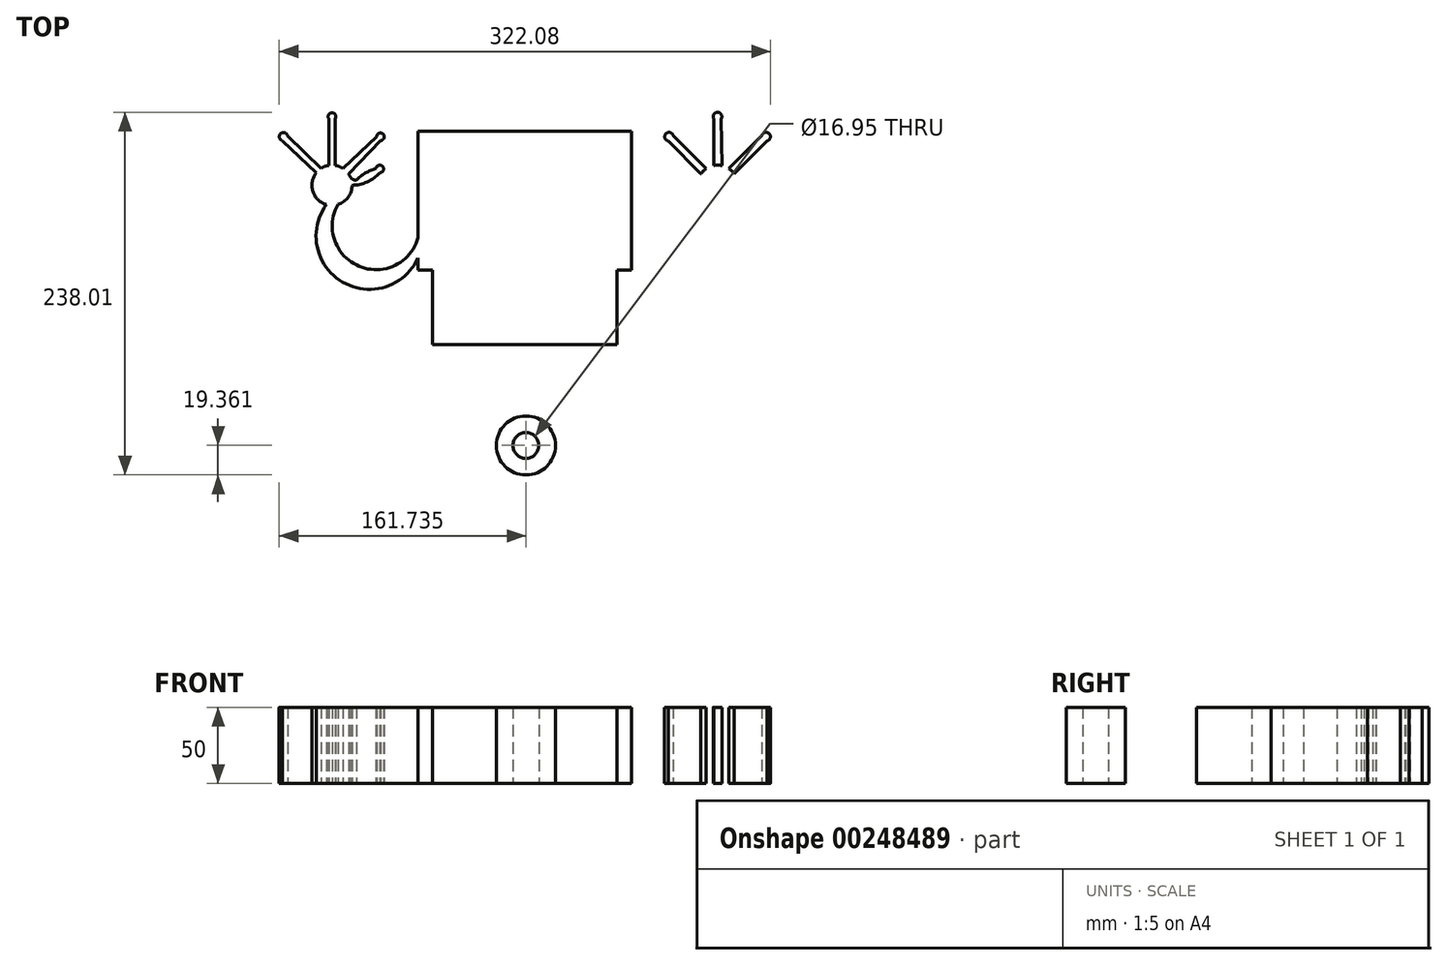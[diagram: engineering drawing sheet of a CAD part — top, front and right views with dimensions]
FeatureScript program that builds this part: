
annotation { "Feature Type Name" : "Feature", "Feature Type Description" : "" }
export const myFeature = defineFeature(function(context is Context, id is Id, definition is map)
    precondition{}
    {
        {
            var Q0;
            Q0=qCreatedBy(makeId("Top.planeOp"),FACE);
            var sketch = newSketch(context, id + "F0", { "sketchPlane" : qUnion([Q0])});
            skLineSegment(sketch, "E0.bottom", {"start": v(-60.5, -70) * mm, "end": v(60.5, -70) * mm});
            skLineSegment(sketch, "E0.top", {"start": v(-70, 70) * mm, "end": v(70, 70) * mm});
            skLineSegment(sketch, "E0.left", {"start": v(-70, -21.2) * mm, "end": v(-70, 70) * mm});
            skLineSegment(sketch, "E0.right", {"start": v(70, -21.2) * mm, "end": v(70, 70) * mm});
            skPoint(sketch, "E0.middle", {"position": v(0, 0) * mm});
            skLineSegment(sketch, "E1", {"start": v(-70, -21.2) * mm, "end": v(-60.5, -21.2) * mm});
            skLineSegment(sketch, "E2", {"start": v(-60.5, -21.2) * mm, "end": v(-60.5, -70) * mm});
            skLineSegment(sketch, "E3", {"start": v(0, -70) * mm, "end": v(0, -30.27) * mm, "construction": true});
            skPoint(sketch, "E3.endSnap0", {"position": v(0, -70) * mm});
            skLineSegment(sketch, "E4.MirrorCS", {"start": v(60.5, -21.2) * mm, "end": v(60.5, -70) * mm});
            skLineSegment(sketch, "E5.MirrorCS", {"start": v(70, -21.2) * mm, "end": v(60.5, -21.2) * mm});
            skArc(sketch, "E6", {"start": v(-130.05, 21.84) * mm, "mid": v(-119.54, -29.05) * mm, "end": v(-70, -13.35) * mm});
            skArc(sketch, "E7", {"start": v(-122.44, 21.94) * mm, "mid": v(-108.64, -18.7) * mm, "end": v(-70, 0) * mm});
            skArc(sketch, "E8.MirrorCS", {"start": v(122.44, 21.94) * mm, "mid": v(108.64, -18.7) * mm, "end": v(70, 0) * mm});
            skArc(sketch, "E9.MirrorCS", {"start": v(130.05, 21.84) * mm, "mid": v(119.54, -29.05) * mm, "end": v(70, -13.35) * mm});
            skLineSegment(sketch, "E10.bottom", {"start": v(-47.81, 17.99) * mm, "end": v(47.81, 17.99) * mm});
            skLineSegment(sketch, "E10.top", {"start": v(-47.81, 60.3) * mm, "end": v(47.81, 60.3) * mm});
            skLineSegment(sketch, "E10.left", {"start": v(-47.81, 17.99) * mm, "end": v(-47.81, 60.3) * mm});
            skLineSegment(sketch, "E10.right", {"start": v(47.81, 17.99) * mm, "end": v(47.81, 60.3) * mm});
            skPoint(sketch, "E10.middle", {"position": v(0, 39.14) * mm});
            skLineSegment(sketch, "E11", {"start": v(-29.12, 60.3) * mm, "end": v(-29.12, 17.99) * mm});
            skLineSegment(sketch, "E12", {"start": v(-10.76, 60.3) * mm, "end": v(-10.36, 17.99) * mm});
            skLineSegment(sketch, "E13", {"start": v(4.52, 60.3) * mm, "end": v(4.52, 17.99) * mm});
            skLineSegment(sketch, "E14", {"start": v(20.03, 17.99) * mm, "end": v(20.03, 60.3) * mm});
            skLineSegment(sketch, "E15", {"start": v(35.65, 60.3) * mm, "end": v(35.65, 17.17) * mm});
            skLineSegment(sketch, "E16", {"start": v(-47.81, 54.52) * mm, "end": v(47.81, 54.52) * mm});
            skLineSegment(sketch, "E17", {"start": v(-47.81, 49.66) * mm, "end": v(47.81, 49.66) * mm});
            skLineSegment(sketch, "E18", {"start": v(-47.81, 44.45) * mm, "end": v(47.81, 44.45) * mm});
            skLineSegment(sketch, "E19", {"start": v(-47.81, 39.14) * mm, "end": v(47.81, 39.14) * mm});
            skLineSegment(sketch, "E20", {"start": v(-47.81, 33.7) * mm, "end": v(47.81, 33.7) * mm});
            skLineSegment(sketch, "E21", {"start": v(-47.81, 28.71) * mm, "end": v(47.81, 28.71) * mm});
            skLineSegment(sketch, "E22", {"start": v(-47.81, 23.4) * mm, "end": v(47.81, 23.4) * mm});
            skLineSegment(sketch, "E23.bottom", {"start": v(-18.12, -13.23) * mm, "end": v(19.82, -13.23) * mm});
            skLineSegment(sketch, "E23.top", {"start": v(-18.12, 1.74) * mm, "end": v(19.82, 1.74) * mm});
            skPoint(sketch, "E23.middle", {"position": v(0, -5.74) * mm});
            skLineSegment(sketch, "E24", {"start": v(-18.12, 1.74) * mm, "end": v(-18.12, -13.23) * mm});
            skLineSegment(sketch, "E25", {"start": v(-4.04, -13.23) * mm, "end": v(-4.04, 1.74) * mm});
            skLineSegment(sketch, "E26", {"start": v(11.61, 1.74) * mm, "end": v(11.61, -13.23) * mm});
            skLineSegment(sketch, "E27", {"start": v(-10.15, 1.74) * mm, "end": v(-10.15, -13.23) * mm});
            skLineSegment(sketch, "E28", {"start": v(-10.15, -13.23) * mm, "end": v(3.76, -13.23) * mm});
            skLineSegment(sketch, "E29", {"start": v(3.76, -13.23) * mm, "end": v(3.76, 1.74) * mm});
            skLineSegment(sketch, "E30", {"start": v(19.82, -13.23) * mm, "end": v(19.82, 1.74) * mm});
            skArc(sketch, "E31", {"start": v(-45.4, -36.02) * mm, "mid": v(-42.59, -55.8) * mm, "end": v(-43.53, -35.84) * mm});
            skArc(sketch, "E32", {"start": v(-23.92, -46.21) * mm, "mid": v(-3.96, -47.19) * mm, "end": v(-23.73, -44.28) * mm});
            skArc(sketch, "E33", {"start": v(21.64, -53.48) * mm, "mid": v(9.32, -37.77) * mm, "end": v(19.59, -54.89) * mm});
            skArc(sketch, "E34", {"start": v(54.53, -45.26) * mm, "mid": v(34.6, -44.16) * mm, "end": v(54.3, -47.43) * mm});
            skLineSegment(sketch, "E35.bottom", {"start": v(-3.17, -70) * mm, "end": v(4.68, -70) * mm});
            skLineSegment(sketch, "E35.left", {"start": v(-3.17, -70) * mm, "end": v(-3.17, -117.33) * mm});
            skLineSegment(sketch, "E35.right", {"start": v(4.68, -70) * mm, "end": v(4.68, -117.33) * mm});
            skCircle(sketch, "E36", {"center": v(0.75, -136.29) * mm, "radius": 19.36 * mm});
            skCircle(sketch, "E37", {"center": v(0.75, -136.29) * mm, "radius": 8.48 * mm});
            skArc(sketch, "E38", {"start": v(-122.44, 21.94) * mm, "mid": v(-126.6, 47.68) * mm, "end": v(-130.05, 21.84) * mm});
            skArc(sketch, "E39.MirrorCS", {"start": v(122.44, 21.94) * mm, "mid": v(126.6, 47.68) * mm, "end": v(130.05, 21.84) * mm});
            skPoint(sketch, "E40.orphan", {"position": v(70, -70) * mm});
            skPoint(sketch, "E41.orphan", {"position": v(-70, -70) * mm});
            skPoint(sketch, "E42.orphan", {"position": v(4.68, -136.29) * mm});
            skPoint(sketch, "E43.orphan", {"position": v(-3.17, -136.29) * mm});
            skLineSegment(sketch, "E44", {"start": v(-43.53, -45.84) * mm, "end": v(-45.4, -36.02) * mm});
            skLineSegment(sketch, "E45", {"start": v(-43.53, -45.84) * mm, "end": v(-43.53, -35.84) * mm});
            skLineSegment(sketch, "E46", {"start": v(-13.92, -46.21) * mm, "end": v(-23.73, -44.28) * mm});
            skLineSegment(sketch, "E47", {"start": v(-13.92, -46.21) * mm, "end": v(-23.92, -46.21) * mm});
            skLineSegment(sketch, "E48", {"start": v(14.99, -46.01) * mm, "end": v(21.64, -53.48) * mm});
            skLineSegment(sketch, "E49", {"start": v(14.99, -46.01) * mm, "end": v(19.59, -54.89) * mm});
            skLineSegment(sketch, "E50", {"start": v(44.53, -45.26) * mm, "end": v(54.53, -45.26) * mm});
            skLineSegment(sketch, "E51", {"start": v(44.53, -45.26) * mm, "end": v(54.3, -47.43) * mm});
            skLineSegment(sketch, "E52", {"start": v(-126.42, 34.5) * mm, "end": v(-139.6, 34.5) * mm, "construction": true});
            skLineSegment(sketch, "E53", {"start": v(-126.42, 34.5) * mm, "end": v(-113.24, 34.5) * mm, "construction": true});
            skLineSegment(sketch, "E54", {"start": v(-126.42, 34.5) * mm, "end": v(-126.42, 79.5) * mm, "construction": true});
            skPoint(sketch, "E55.endSnap0", {"position": v(-126.6, 47.68) * mm});
            skLineSegment(sketch, "E56", {"start": v(-126.42, 34.5) * mm, "end": v(-158.24, 66.32) * mm, "construction": true});
            skLineSegment(sketch, "E57", {"start": v(-126.42, 34.5) * mm, "end": v(-94.6, 66.32) * mm, "construction": true});
            skLineSegment(sketch, "E58.MirrorCS", {"start": v(126.42, 34.5) * mm, "end": v(94.6, 66.32) * mm, "construction": true});
            skLineSegment(sketch, "E59.MirrorCS", {"start": v(126.42, 34.5) * mm, "end": v(113.24, 34.5) * mm, "construction": true});
            skLineSegment(sketch, "E60.MirrorCS", {"start": v(126.42, 34.5) * mm, "end": v(126.42, 79.5) * mm, "construction": true});
            skLineSegment(sketch, "E61.MirrorCS", {"start": v(126.42, 34.5) * mm, "end": v(158.24, 66.32) * mm, "construction": true});
            skLineSegment(sketch, "E62.MirrorCS", {"start": v(126.42, 34.5) * mm, "end": v(139.6, 34.5) * mm, "construction": true});
            skArc(sketch, "E63", {"start": v(-94.33, 63.85) * mm, "mid": v(-92.86, 68.1) * mm, "end": v(-97.08, 66.52) * mm});
            skArc(sketch, "E64", {"start": v(-124.4, 78) * mm, "mid": v(-126.42, 82.02) * mm, "end": v(-128.44, 78) * mm});
            skArc(sketch, "E65", {"start": v(-155.52, 66.73) * mm, "mid": v(-160.1, 68.34) * mm, "end": v(-158.87, 63.65) * mm});
            skLineSegment(sketch, "E66", {"start": v(-97.08, 66.52) * mm, "end": v(-119.13, 45.48) * mm});
            skLineSegment(sketch, "E67", {"start": v(-94.33, 63.85) * mm, "end": v(-115.57, 41.98) * mm});
            skLineSegment(sketch, "E68", {"start": v(-124.4, 78) * mm, "end": v(-124.4, 47.52) * mm});
            skLineSegment(sketch, "E69", {"start": v(-128.44, 78) * mm, "end": v(-128.44, 47.52) * mm});
            skLineSegment(sketch, "E70", {"start": v(-155.52, 66.73) * mm, "end": v(-133.62, 45.54) * mm});
            skLineSegment(sketch, "E71", {"start": v(-158.87, 63.65) * mm, "end": v(-136.7, 42.73) * mm});
            skArc(sketch, "E72", {"start": v(158.82, 63.52) * mm, "mid": v(160.26, 68.34) * mm, "end": v(155.44, 66.9) * mm});
            skArc(sketch, "E73", {"start": v(128.7, 77.8) * mm, "mid": v(126.5, 82.36) * mm, "end": v(124.02, 77.94) * mm});
            skArc(sketch, "E74", {"start": v(97.4, 66.9) * mm, "mid": v(92.56, 68.33) * mm, "end": v(94.05, 63.52) * mm});
            skLineSegment(sketch, "E75", {"start": v(158.82, 63.52) * mm, "end": v(137.27, 41.97) * mm});
            skLineSegment(sketch, "E76", {"start": v(155.44, 66.9) * mm, "end": v(133.89, 45.36) * mm});
            skLineSegment(sketch, "E77", {"start": v(128.7, 77.8) * mm, "end": v(129.45, 47.32) * mm});
            skLineSegment(sketch, "E78", {"start": v(124.02, 77.94) * mm, "end": v(124.02, 47.46) * mm});
            skLineSegment(sketch, "E79", {"start": v(97.4, 66.9) * mm, "end": v(118.95, 45.36) * mm});
            skLineSegment(sketch, "E80", {"start": v(94.05, 63.52) * mm, "end": v(115.47, 41.84) * mm});
            skPoint(sketch, "E23.right.start.orphan", {"position": v(31.02, -13.23) * mm});
            skPoint(sketch, "E81.orphan", {"position": v(31.02, 1.74) * mm});
            skPoint(sketch, "E23.left.end.orphan", {"position": v(-31.02, 1.74) * mm});
            skPoint(sketch, "E82.orphan", {"position": v(-31.02, -13.23) * mm});
            skLineSegment(sketch, "E83", {"start": v(-113.24, 34.5) * mm, "end": v(-95.06, 45.17) * mm, "construction": true});
            skArc(sketch, "E84", {"start": v(-95.1, 42.68) * mm, "mid": v(-93.21, 46.84) * mm, "end": v(-97.54, 45.38) * mm});
            skArc(sketch, "E85", {"start": v(-97.54, 45.38) * mm, "mid": v(-104.46, 42.48) * mm, "end": v(-110.4, 37.87) * mm});
            skArc(sketch, "E86", {"start": v(-113.24, 34.5) * mm, "mid": v(-103.29, 36.64) * mm, "end": v(-95.1, 42.68) * mm});
            skArc(sketch, "E87", {"start": v(-114.29, 39.65) * mm, "mid": v(-112.57, 38.25) * mm, "end": v(-110.4, 37.87) * mm});
            skArc(sketch, "E88.MirrorCS", {"start": v(113.24, 34.5) * mm, "mid": v(103.29, 36.64) * mm, "end": v(95.1, 42.68) * mm});
            skArc(sketch, "E89.MirrorC", {"start": v(95.1, 42.68) * mm, "mid": v(93.21, 46.84) * mm, "end": v(97.54, 45.38) * mm});
            skArc(sketch, "E90.MirrorCS", {"start": v(97.54, 45.38) * mm, "mid": v(104.46, 42.48) * mm, "end": v(110.4, 37.87) * mm});
            skArc(sketch, "E91.MirrorCS", {"start": v(114.29, 39.65) * mm, "mid": v(112.57, 38.25) * mm, "end": v(110.4, 37.87) * mm});
            skSolve(sketch);
        }
        {
            var Q0;
            {var subQ3=sQuery(id+"F0.wireOp",EDGE,"E6");Q0=makeQuery(id+"F0.imprint","IMPRINT",FACE,{"disambiguationData":[TD([[makeQuery(id+"F0.imprint","IMPRINT",EDGE,{"derivedFrom":subQ3}),1.0]])]});}
            var Q1;
            {var subQ24=sQuery(id+"F0.wireOp",EDGE,"E0.top");Q1=makeQuery(id+"F0.imprint","IMPRINT",FACE,{"disambiguationData":[TD([[makeQuery(id+"F0.imprint","IMPRINT",EDGE,{"derivedFrom":subQ24}),-1.0]])]});}
            var Q2;
            {var subQ8=sQuery(id+"F0.wireOp",EDGE,"E8.MirrorCS");Q2=makeQuery(id+"F0.imprint","IMPRINT",FACE,{"disambiguationData":[TD([[makeQuery(id+"F0.imprint","IMPRINT",EDGE,{"derivedFrom":subQ8}),1.0]])]});}
            var Q3;
            {var subQ1=sQuery(id+"F0.wireOp",EDGE,"E88.MirrorCS");Q3=makeQuery(id+"F0.imprint","IMPRINT",FACE,{"disambiguationData":[TD([[makeQuery(id+"F0.imprint","IMPRINT",EDGE,{"derivedFrom":subQ1}),-1.0]])]});}
            var Q4;
            Q4=makeQuery(id+"F0.imprint","IMPRINT",FACE,{"disambiguationData":[TD([[makeQuery(id+"F0.imprint","IMPRINT",EDGE,{"derivedFrom":sQuery(id+"F0.wireOp",EDGE,"E74")}),1.0]])]});
            var Q5;
            Q5=makeQuery(id+"F0.imprint","IMPRINT",FACE,{"disambiguationData":[TD([[makeQuery(id+"F0.imprint","IMPRINT",EDGE,{"derivedFrom":sQuery(id+"F0.wireOp",EDGE,"E73")}),1.0]])]});
            var Q6;
            Q6=makeQuery(id+"F0.imprint","IMPRINT",FACE,{"disambiguationData":[TD([[makeQuery(id+"F0.imprint","IMPRINT",EDGE,{"derivedFrom":sQuery(id+"F0.wireOp",EDGE,"E72")}),1.0]])]});
            var Q7;
            Q7=makeQuery(id+"F0.imprint","IMPRINT",FACE,{"disambiguationData":[TD([[makeQuery(id+"F0.imprint","IMPRINT",EDGE,{"derivedFrom":sQuery(id+"F0.wireOp",EDGE,"E65")}),1.0]])]});
            var Q8;
            Q8=makeQuery(id+"F0.imprint","IMPRINT",FACE,{"disambiguationData":[TD([[makeQuery(id+"F0.imprint","IMPRINT",EDGE,{"derivedFrom":sQuery(id+"F0.wireOp",EDGE,"E64")}),1.0]])]});
            var Q9;
            Q9=makeQuery(id+"F0.imprint","IMPRINT",FACE,{"disambiguationData":[TD([[makeQuery(id+"F0.imprint","IMPRINT",EDGE,{"derivedFrom":sQuery(id+"F0.wireOp",EDGE,"E63")}),1.0]])]});
            var Q10;
            Q10=makeQuery(id+"F0.imprint","IMPRINT",FACE,{"disambiguationData":[TD([[makeQuery(id+"F0.imprint","IMPRINT",EDGE,{"derivedFrom":sQuery(id+"F0.wireOp",EDGE,"E84")}),1.0]])]});
            var Q11;
            Q11=makeQuery(id+"F0.imprint","IMPRINT",FACE,{"disambiguationData":[TD([[makeQuery(id+"F0.imprint","IMPRINT",EDGE,{"derivedFrom":sQuery(id+"F0.wireOp",EDGE,"E31")}),1.0]])]});
            var Q12;
            Q12=makeQuery(id+"F0.imprint","IMPRINT",FACE,{"disambiguationData":[TD([[makeQuery(id+"F0.imprint","IMPRINT",EDGE,{"derivedFrom":sQuery(id+"F0.wireOp",EDGE,"E32")}),1.0]])]});
            var Q13;
            Q13=makeQuery(id+"F0.imprint","IMPRINT",FACE,{"disambiguationData":[TD([[makeQuery(id+"F0.imprint","IMPRINT",EDGE,{"derivedFrom":sQuery(id+"F0.wireOp",EDGE,"E33")}),1.0]])]});
            var Q14;
            Q14=makeQuery(id+"F0.imprint","IMPRINT",FACE,{"disambiguationData":[TD([[makeQuery(id+"F0.imprint","IMPRINT",EDGE,{"derivedFrom":sQuery(id+"F0.wireOp",EDGE,"E34")}),1.0]])]});
            var Q15;
            {var subQ2=sQuery(id+"F0.wireOp",EDGE,"E26");Q15=makeQuery(id+"F0.imprint","IMPRINT",FACE,{"disambiguationData":[TD([[makeQuery(id+"F0.imprint","IMPRINT",EDGE,{"derivedFrom":subQ2}),1.0]])]});}
            var Q16;
            {var subQ0=sQuery(id+"F0.wireOp",EDGE,"E26");Q16=makeQuery(id+"F0.imprint","IMPRINT",FACE,{"disambiguationData":[TD([[makeQuery(id+"F0.imprint","IMPRINT",EDGE,{"derivedFrom":subQ0}),-1.0]])]});}
            var Q17;
            {var subQ0=sQuery(id+"F0.wireOp",EDGE,"E25");Q17=makeQuery(id+"F0.imprint","IMPRINT",FACE,{"disambiguationData":[TD([[makeQuery(id+"F0.imprint","IMPRINT",EDGE,{"derivedFrom":subQ0}),1.0]])]});}
            var Q18;
            {var subQ0=sQuery(id+"F0.wireOp",EDGE,"E24");Q18=makeQuery(id+"F0.imprint","IMPRINT",FACE,{"disambiguationData":[TD([[makeQuery(id+"F0.imprint","IMPRINT",EDGE,{"derivedFrom":subQ0}),1.0]])]});}
            var Q19;
            {var subQ0=sQuery(id+"F0.wireOp",EDGE,"E25");Q19=makeQuery(id+"F0.imprint","IMPRINT",FACE,{"disambiguationData":[TD([[makeQuery(id+"F0.imprint","IMPRINT",EDGE,{"derivedFrom":subQ0}),-1.0]])]});}
            var Q20;
            Q20=makeQuery(id+"F0.imprint","IMPRINT",FACE,{"disambiguationData":[TD([[makeQuery(id+"F0.imprint","IMPRINT",EDGE,{"derivedFrom":sQuery(id+"F0.wireOp",EDGE,"E35.bottom")}),-1.0]])]});
            var Q21;
            Q21=makeQuery(id+"F0.imprint","IMPRINT",FACE,{"disambiguationData":[TD([[makeQuery(id+"F0.imprint","IMPRINT",EDGE,{"derivedFrom":sQuery(id+"F0.wireOp",EDGE,"E37")}),-1.0]])]});
            var Q22;
            {var subQ0=sQuery(id+"F0.wireOp",EDGE,"E18");var subQ1=sQuery(id+"F0.wireOp",EDGE,"E10.right");var subQ2=makeQuery(id+"F0.imprint","INTERSECT",VERTEX,{"derivedFrom":[subQ1,subQ0]});Q22=makeQuery(id+"F0.imprint","IMPRINT",FACE,{"disambiguationData":[TD([[makeQuery(id+"F0.imprint","IMPRINT",EDGE,{"disambiguationData":[TD([[subQ2,1.0]])],"derivedFrom":subQ1}),1.0]])]});}
            var Q23;
            {var subQ0=sQuery(id+"F0.wireOp",EDGE,"E21");var subQ1=sQuery(id+"F0.wireOp",EDGE,"E14");var subQ2=makeQuery(id+"F0.imprint","INTERSECT",VERTEX,{"derivedFrom":[subQ1,subQ0]});Q23=makeQuery(id+"F0.imprint","IMPRINT",FACE,{"disambiguationData":[TD([[makeQuery(id+"F0.imprint","IMPRINT",EDGE,{"disambiguationData":[TD([[subQ2,-1.0]])],"derivedFrom":subQ1}),-1.0]])]});}
            var Q24;
            {var subQ0=sQuery(id+"F0.wireOp",EDGE,"E21");var subQ1=sQuery(id+"F0.wireOp",EDGE,"E10.left");var subQ2=makeQuery(id+"F0.imprint","INTERSECT",VERTEX,{"derivedFrom":[subQ1,subQ0]});Q24=makeQuery(id+"F0.imprint","IMPRINT",FACE,{"disambiguationData":[TD([[makeQuery(id+"F0.imprint","IMPRINT",EDGE,{"disambiguationData":[TD([[subQ2,1.0]])],"derivedFrom":subQ1}),-1.0]])]});}
            var Q25;
            {var subQ0=sQuery(id+"F0.wireOp",EDGE,"E20");var subQ1=sQuery(id+"F0.wireOp",EDGE,"E12");var subQ2=makeQuery(id+"F0.imprint","INTERSECT",VERTEX,{"derivedFrom":[subQ1,subQ0]});Q25=makeQuery(id+"F0.imprint","IMPRINT",FACE,{"disambiguationData":[TD([[makeQuery(id+"F0.imprint","IMPRINT",EDGE,{"disambiguationData":[TD([[subQ2,-1.0]])],"derivedFrom":subQ1}),1.0]])]});}
            var Q26;
            {var subQ0=sQuery(id+"F0.wireOp",EDGE,"E20");var subQ1=sQuery(id+"F0.wireOp",EDGE,"E14");var subQ2=makeQuery(id+"F0.imprint","INTERSECT",VERTEX,{"derivedFrom":[subQ1,subQ0]});Q26=makeQuery(id+"F0.imprint","IMPRINT",FACE,{"disambiguationData":[TD([[makeQuery(id+"F0.imprint","IMPRINT",EDGE,{"disambiguationData":[TD([[subQ2,-1.0]])],"derivedFrom":subQ1}),-1.0]])]});}
            var Q27;
            {var subQ0=sQuery(id+"F0.wireOp",EDGE,"E14");var subQ1=sQuery(id+"F0.wireOp",EDGE,"E10.top");var subQ2=makeQuery(id+"F0.imprint","INTERSECT",VERTEX,{"derivedFrom":[subQ1,subQ0]});Q27=makeQuery(id+"F0.imprint","IMPRINT",FACE,{"disambiguationData":[TD([[makeQuery(id+"F0.imprint","IMPRINT",EDGE,{"disambiguationData":[TD([[subQ2,-1.0]])],"derivedFrom":subQ1}),-1.0]])]});}
            var Q28;
            {var subQ0=sQuery(id+"F0.wireOp",EDGE,"E20");var subQ1=sQuery(id+"F0.wireOp",EDGE,"E11");var subQ2=makeQuery(id+"F0.imprint","INTERSECT",VERTEX,{"derivedFrom":[subQ1,subQ0]});Q28=makeQuery(id+"F0.imprint","IMPRINT",FACE,{"disambiguationData":[TD([[makeQuery(id+"F0.imprint","IMPRINT",EDGE,{"disambiguationData":[TD([[subQ2,-1.0]])],"derivedFrom":subQ1}),1.0]])]});}
            var Q29;
            {var subQ0=sQuery(id+"F0.wireOp",EDGE,"E21");var subQ1=sQuery(id+"F0.wireOp",EDGE,"E10.right");var subQ2=makeQuery(id+"F0.imprint","INTERSECT",VERTEX,{"derivedFrom":[subQ1,subQ0]});Q29=makeQuery(id+"F0.imprint","IMPRINT",FACE,{"disambiguationData":[TD([[makeQuery(id+"F0.imprint","IMPRINT",EDGE,{"disambiguationData":[TD([[subQ2,1.0]])],"derivedFrom":subQ1}),1.0]])]});}
            var Q30;
            {var subQ0=sQuery(id+"F0.wireOp",EDGE,"E12");var subQ1=sQuery(id+"F0.wireOp",EDGE,"E10.bottom");var subQ2=makeQuery(id+"F0.imprint","INTERSECT",VERTEX,{"derivedFrom":[subQ1,subQ0]});Q30=makeQuery(id+"F0.imprint","IMPRINT",FACE,{"disambiguationData":[TD([[makeQuery(id+"F0.imprint","IMPRINT",EDGE,{"disambiguationData":[TD([[subQ2,-1.0]])],"derivedFrom":subQ1}),1.0]])]});}
            var Q31;
            {var subQ0=sQuery(id+"F0.wireOp",EDGE,"E11");var subQ1=sQuery(id+"F0.wireOp",EDGE,"E10.bottom");var subQ2=makeQuery(id+"F0.imprint","INTERSECT",VERTEX,{"derivedFrom":[subQ1,subQ0]});Q31=makeQuery(id+"F0.imprint","IMPRINT",FACE,{"disambiguationData":[TD([[makeQuery(id+"F0.imprint","IMPRINT",EDGE,{"disambiguationData":[TD([[subQ2,-1.0]])],"derivedFrom":subQ1}),1.0]])]});}
            var Q32;
            {var subQ0=sQuery(id+"F0.wireOp",EDGE,"E11");var subQ1=sQuery(id+"F0.wireOp",EDGE,"E10.top");var subQ2=makeQuery(id+"F0.imprint","INTERSECT",VERTEX,{"derivedFrom":[subQ1,subQ0]});Q32=makeQuery(id+"F0.imprint","IMPRINT",FACE,{"disambiguationData":[TD([[makeQuery(id+"F0.imprint","IMPRINT",EDGE,{"disambiguationData":[TD([[subQ2,-1.0]])],"derivedFrom":subQ1}),-1.0]])]});}
            var Q33;
            {var subQ0=sQuery(id+"F0.wireOp",EDGE,"E16");var subQ1=sQuery(id+"F0.wireOp",EDGE,"E11");var subQ2=makeQuery(id+"F0.imprint","INTERSECT",VERTEX,{"derivedFrom":[subQ1,subQ0]});Q33=makeQuery(id+"F0.imprint","IMPRINT",FACE,{"disambiguationData":[TD([[makeQuery(id+"F0.imprint","IMPRINT",EDGE,{"disambiguationData":[TD([[subQ2,-1.0]])],"derivedFrom":subQ1}),1.0]])]});}
            var Q34;
            {var subQ0=sQuery(id+"F0.wireOp",EDGE,"E20");var subQ1=sQuery(id+"F0.wireOp",EDGE,"E13");var subQ2=makeQuery(id+"F0.imprint","INTERSECT",VERTEX,{"derivedFrom":[subQ1,subQ0]});Q34=makeQuery(id+"F0.imprint","IMPRINT",FACE,{"disambiguationData":[TD([[makeQuery(id+"F0.imprint","IMPRINT",EDGE,{"disambiguationData":[TD([[subQ2,-1.0]])],"derivedFrom":subQ1}),1.0]])]});}
            var Q35;
            {var subQ0=sQuery(id+"F0.wireOp",EDGE,"E19");var subQ1=sQuery(id+"F0.wireOp",EDGE,"E14");var subQ2=makeQuery(id+"F0.imprint","INTERSECT",VERTEX,{"derivedFrom":[subQ1,subQ0]});Q35=makeQuery(id+"F0.imprint","IMPRINT",FACE,{"disambiguationData":[TD([[makeQuery(id+"F0.imprint","IMPRINT",EDGE,{"disambiguationData":[TD([[subQ2,-1.0]])],"derivedFrom":subQ1}),-1.0]])]});}
            var Q36;
            {var subQ0=sQuery(id+"F0.wireOp",EDGE,"E19");var subQ1=sQuery(id+"F0.wireOp",EDGE,"E11");var subQ2=makeQuery(id+"F0.imprint","INTERSECT",VERTEX,{"derivedFrom":[subQ1,subQ0]});Q36=makeQuery(id+"F0.imprint","IMPRINT",FACE,{"disambiguationData":[TD([[makeQuery(id+"F0.imprint","IMPRINT",EDGE,{"disambiguationData":[TD([[subQ2,-1.0]])],"derivedFrom":subQ1}),1.0]])]});}
            var Q37;
            {var subQ0=sQuery(id+"F0.wireOp",EDGE,"E17");var subQ1=sQuery(id+"F0.wireOp",EDGE,"E13");var subQ2=makeQuery(id+"F0.imprint","INTERSECT",VERTEX,{"derivedFrom":[subQ1,subQ0]});Q37=makeQuery(id+"F0.imprint","IMPRINT",FACE,{"disambiguationData":[TD([[makeQuery(id+"F0.imprint","IMPRINT",EDGE,{"disambiguationData":[TD([[subQ2,-1.0]])],"derivedFrom":subQ1}),1.0]])]});}
            var Q38;
            {var subQ0=sQuery(id+"F0.wireOp",EDGE,"E20");var subQ1=sQuery(id+"F0.wireOp",EDGE,"E10.right");var subQ2=makeQuery(id+"F0.imprint","INTERSECT",VERTEX,{"derivedFrom":[subQ1,subQ0]});Q38=makeQuery(id+"F0.imprint","IMPRINT",FACE,{"disambiguationData":[TD([[makeQuery(id+"F0.imprint","IMPRINT",EDGE,{"disambiguationData":[TD([[subQ2,1.0]])],"derivedFrom":subQ1}),1.0]])]});}
            var Q39;
            {var subQ0=sQuery(id+"F0.wireOp",EDGE,"E20");var subQ1=sQuery(id+"F0.wireOp",EDGE,"E10.left");var subQ2=makeQuery(id+"F0.imprint","INTERSECT",VERTEX,{"derivedFrom":[subQ1,subQ0]});Q39=makeQuery(id+"F0.imprint","IMPRINT",FACE,{"disambiguationData":[TD([[makeQuery(id+"F0.imprint","IMPRINT",EDGE,{"disambiguationData":[TD([[subQ2,1.0]])],"derivedFrom":subQ1}),-1.0]])]});}
            var Q40;
            {var subQ0=sQuery(id+"F0.wireOp",EDGE,"E16");var subQ1=sQuery(id+"F0.wireOp",EDGE,"E12");var subQ2=makeQuery(id+"F0.imprint","INTERSECT",VERTEX,{"derivedFrom":[subQ1,subQ0]});Q40=makeQuery(id+"F0.imprint","IMPRINT",FACE,{"disambiguationData":[TD([[makeQuery(id+"F0.imprint","IMPRINT",EDGE,{"disambiguationData":[TD([[subQ2,-1.0]])],"derivedFrom":subQ1}),1.0]])]});}
            var Q41;
            {var subQ0=sQuery(id+"F0.wireOp",EDGE,"E16");var subQ1=sQuery(id+"F0.wireOp",EDGE,"E13");var subQ2=makeQuery(id+"F0.imprint","INTERSECT",VERTEX,{"derivedFrom":[subQ1,subQ0]});Q41=makeQuery(id+"F0.imprint","IMPRINT",FACE,{"disambiguationData":[TD([[makeQuery(id+"F0.imprint","IMPRINT",EDGE,{"disambiguationData":[TD([[subQ2,-1.0]])],"derivedFrom":subQ1}),1.0]])]});}
            var Q42;
            {var subQ0=sQuery(id+"F0.wireOp",EDGE,"E19");var subQ1=sQuery(id+"F0.wireOp",EDGE,"E10.left");var subQ2=makeQuery(id+"F0.imprint","INTERSECT",VERTEX,{"derivedFrom":[subQ1,subQ0]});Q42=makeQuery(id+"F0.imprint","IMPRINT",FACE,{"disambiguationData":[TD([[makeQuery(id+"F0.imprint","IMPRINT",EDGE,{"disambiguationData":[TD([[subQ2,1.0]])],"derivedFrom":subQ1}),-1.0]])]});}
            var Q43;
            {var subQ0=sQuery(id+"F0.wireOp",EDGE,"E18");var subQ1=sQuery(id+"F0.wireOp",EDGE,"E14");var subQ2=makeQuery(id+"F0.imprint","INTERSECT",VERTEX,{"derivedFrom":[subQ1,subQ0]});Q43=makeQuery(id+"F0.imprint","IMPRINT",FACE,{"disambiguationData":[TD([[makeQuery(id+"F0.imprint","IMPRINT",EDGE,{"disambiguationData":[TD([[subQ2,-1.0]])],"derivedFrom":subQ1}),-1.0]])]});}
            var Q44;
            {var subQ0=sQuery(id+"F0.wireOp",EDGE,"E21");var subQ1=sQuery(id+"F0.wireOp",EDGE,"E11");var subQ2=makeQuery(id+"F0.imprint","INTERSECT",VERTEX,{"derivedFrom":[subQ1,subQ0]});Q44=makeQuery(id+"F0.imprint","IMPRINT",FACE,{"disambiguationData":[TD([[makeQuery(id+"F0.imprint","IMPRINT",EDGE,{"disambiguationData":[TD([[subQ2,-1.0]])],"derivedFrom":subQ1}),1.0]])]});}
            var Q45;
            {var subQ0=sQuery(id+"F0.wireOp",EDGE,"E19");var subQ1=sQuery(id+"F0.wireOp",EDGE,"E10.right");var subQ2=makeQuery(id+"F0.imprint","INTERSECT",VERTEX,{"derivedFrom":[subQ1,subQ0]});Q45=makeQuery(id+"F0.imprint","IMPRINT",FACE,{"disambiguationData":[TD([[makeQuery(id+"F0.imprint","IMPRINT",EDGE,{"disambiguationData":[TD([[subQ2,1.0]])],"derivedFrom":subQ1}),1.0]])]});}
            var Q46;
            {var subQ0=sQuery(id+"F0.wireOp",EDGE,"E10.right");var subQ1=sQuery(id+"F0.wireOp",EDGE,"E10.bottom");var subQ2=makeQuery(id+"F0.imprint","INTERSECT",VERTEX,{"derivedFrom":[subQ1,subQ0]});Q46=makeQuery(id+"F0.imprint","IMPRINT",FACE,{"disambiguationData":[TD([[makeQuery(id+"F0.imprint","IMPRINT",EDGE,{"disambiguationData":[TD([[subQ2,1.0]])],"derivedFrom":subQ1}),1.0]])]});}
            var Q47;
            {var subQ0=sQuery(id+"F0.wireOp",EDGE,"E21");var subQ1=sQuery(id+"F0.wireOp",EDGE,"E12");var subQ2=makeQuery(id+"F0.imprint","INTERSECT",VERTEX,{"derivedFrom":[subQ1,subQ0]});Q47=makeQuery(id+"F0.imprint","IMPRINT",FACE,{"disambiguationData":[TD([[makeQuery(id+"F0.imprint","IMPRINT",EDGE,{"disambiguationData":[TD([[subQ2,-1.0]])],"derivedFrom":subQ1}),1.0]])]});}
            var Q48;
            {var subQ0=sQuery(id+"F0.wireOp",EDGE,"E10.left");var subQ1=sQuery(id+"F0.wireOp",EDGE,"E10.bottom");var subQ2=makeQuery(id+"F0.imprint","INTERSECT",VERTEX,{"derivedFrom":[subQ1,subQ0]});Q48=makeQuery(id+"F0.imprint","IMPRINT",FACE,{"disambiguationData":[TD([[makeQuery(id+"F0.imprint","IMPRINT",EDGE,{"disambiguationData":[TD([[subQ2,-1.0]])],"derivedFrom":subQ1}),1.0]])]});}
            var Q49;
            {var subQ0=sQuery(id+"F0.wireOp",EDGE,"E12");var subQ1=sQuery(id+"F0.wireOp",EDGE,"E10.top");var subQ2=makeQuery(id+"F0.imprint","INTERSECT",VERTEX,{"derivedFrom":[subQ1,subQ0]});Q49=makeQuery(id+"F0.imprint","IMPRINT",FACE,{"disambiguationData":[TD([[makeQuery(id+"F0.imprint","IMPRINT",EDGE,{"disambiguationData":[TD([[subQ2,-1.0]])],"derivedFrom":subQ1}),-1.0]])]});}
            var Q50;
            {var subQ0=sQuery(id+"F0.wireOp",EDGE,"E17");var subQ1=sQuery(id+"F0.wireOp",EDGE,"E10.right");var subQ2=makeQuery(id+"F0.imprint","INTERSECT",VERTEX,{"derivedFrom":[subQ1,subQ0]});Q50=makeQuery(id+"F0.imprint","IMPRINT",FACE,{"disambiguationData":[TD([[makeQuery(id+"F0.imprint","IMPRINT",EDGE,{"disambiguationData":[TD([[subQ2,1.0]])],"derivedFrom":subQ1}),1.0]])]});}
            var Q51;
            {var subQ0=sQuery(id+"F0.wireOp",EDGE,"E13");var subQ1=sQuery(id+"F0.wireOp",EDGE,"E10.bottom");var subQ2=makeQuery(id+"F0.imprint","INTERSECT",VERTEX,{"derivedFrom":[subQ1,subQ0]});Q51=makeQuery(id+"F0.imprint","IMPRINT",FACE,{"disambiguationData":[TD([[makeQuery(id+"F0.imprint","IMPRINT",EDGE,{"disambiguationData":[TD([[subQ2,-1.0]])],"derivedFrom":subQ1}),1.0]])]});}
            var Q52;
            {var subQ0=sQuery(id+"F0.wireOp",EDGE,"E16");var subQ1=sQuery(id+"F0.wireOp",EDGE,"E10.right");var subQ2=makeQuery(id+"F0.imprint","INTERSECT",VERTEX,{"derivedFrom":[subQ1,subQ0]});Q52=makeQuery(id+"F0.imprint","IMPRINT",FACE,{"disambiguationData":[TD([[makeQuery(id+"F0.imprint","IMPRINT",EDGE,{"disambiguationData":[TD([[subQ2,1.0]])],"derivedFrom":subQ1}),1.0]])]});}
            var Q53;
            {var subQ0=sQuery(id+"F0.wireOp",EDGE,"E14");var subQ1=sQuery(id+"F0.wireOp",EDGE,"E10.bottom");var subQ2=makeQuery(id+"F0.imprint","INTERSECT",VERTEX,{"derivedFrom":[subQ1,subQ0]});Q53=makeQuery(id+"F0.imprint","IMPRINT",FACE,{"disambiguationData":[TD([[makeQuery(id+"F0.imprint","IMPRINT",EDGE,{"disambiguationData":[TD([[subQ2,-1.0]])],"derivedFrom":subQ1}),1.0]])]});}
            var Q54;
            {var subQ0=sQuery(id+"F0.wireOp",EDGE,"E17");var subQ1=sQuery(id+"F0.wireOp",EDGE,"E14");var subQ2=makeQuery(id+"F0.imprint","INTERSECT",VERTEX,{"derivedFrom":[subQ1,subQ0]});Q54=makeQuery(id+"F0.imprint","IMPRINT",FACE,{"disambiguationData":[TD([[makeQuery(id+"F0.imprint","IMPRINT",EDGE,{"disambiguationData":[TD([[subQ2,-1.0]])],"derivedFrom":subQ1}),-1.0]])]});}
            var Q55;
            {var subQ0=sQuery(id+"F0.wireOp",EDGE,"E18");var subQ1=sQuery(id+"F0.wireOp",EDGE,"E10.left");var subQ2=makeQuery(id+"F0.imprint","INTERSECT",VERTEX,{"derivedFrom":[subQ1,subQ0]});Q55=makeQuery(id+"F0.imprint","IMPRINT",FACE,{"disambiguationData":[TD([[makeQuery(id+"F0.imprint","IMPRINT",EDGE,{"disambiguationData":[TD([[subQ2,1.0]])],"derivedFrom":subQ1}),-1.0]])]});}
            var Q56;
            {var subQ0=sQuery(id+"F0.wireOp",EDGE,"E10.right");var subQ1=sQuery(id+"F0.wireOp",EDGE,"E10.top");var subQ2=makeQuery(id+"F0.imprint","INTERSECT",VERTEX,{"derivedFrom":[subQ1,subQ0]});Q56=makeQuery(id+"F0.imprint","IMPRINT",FACE,{"disambiguationData":[TD([[makeQuery(id+"F0.imprint","IMPRINT",EDGE,{"disambiguationData":[TD([[subQ2,1.0]])],"derivedFrom":subQ1}),-1.0]])]});}
            var Q57;
            {var subQ0=sQuery(id+"F0.wireOp",EDGE,"E13");var subQ1=sQuery(id+"F0.wireOp",EDGE,"E10.top");var subQ2=makeQuery(id+"F0.imprint","INTERSECT",VERTEX,{"derivedFrom":[subQ1,subQ0]});Q57=makeQuery(id+"F0.imprint","IMPRINT",FACE,{"disambiguationData":[TD([[makeQuery(id+"F0.imprint","IMPRINT",EDGE,{"disambiguationData":[TD([[subQ2,-1.0]])],"derivedFrom":subQ1}),-1.0]])]});}
            var Q58;
            {var subQ0=sQuery(id+"F0.wireOp",EDGE,"E21");var subQ1=sQuery(id+"F0.wireOp",EDGE,"E13");var subQ2=makeQuery(id+"F0.imprint","INTERSECT",VERTEX,{"derivedFrom":[subQ1,subQ0]});Q58=makeQuery(id+"F0.imprint","IMPRINT",FACE,{"disambiguationData":[TD([[makeQuery(id+"F0.imprint","IMPRINT",EDGE,{"disambiguationData":[TD([[subQ2,-1.0]])],"derivedFrom":subQ1}),1.0]])]});}
            var Q59;
            {var subQ0=sQuery(id+"F0.wireOp",EDGE,"E10.left");var subQ1=sQuery(id+"F0.wireOp",EDGE,"E10.top");var subQ2=makeQuery(id+"F0.imprint","INTERSECT",VERTEX,{"derivedFrom":[subQ1,subQ0]});Q59=makeQuery(id+"F0.imprint","IMPRINT",FACE,{"disambiguationData":[TD([[makeQuery(id+"F0.imprint","IMPRINT",EDGE,{"disambiguationData":[TD([[subQ2,-1.0]])],"derivedFrom":subQ1}),-1.0]])]});}
            var Q60;
            {var subQ0=sQuery(id+"F0.wireOp",EDGE,"E17");var subQ1=sQuery(id+"F0.wireOp",EDGE,"E11");var subQ2=makeQuery(id+"F0.imprint","INTERSECT",VERTEX,{"derivedFrom":[subQ1,subQ0]});Q60=makeQuery(id+"F0.imprint","IMPRINT",FACE,{"disambiguationData":[TD([[makeQuery(id+"F0.imprint","IMPRINT",EDGE,{"disambiguationData":[TD([[subQ2,-1.0]])],"derivedFrom":subQ1}),1.0]])]});}
            var Q61;
            {var subQ0=sQuery(id+"F0.wireOp",EDGE,"E17");var subQ1=sQuery(id+"F0.wireOp",EDGE,"E12");var subQ2=makeQuery(id+"F0.imprint","INTERSECT",VERTEX,{"derivedFrom":[subQ1,subQ0]});Q61=makeQuery(id+"F0.imprint","IMPRINT",FACE,{"disambiguationData":[TD([[makeQuery(id+"F0.imprint","IMPRINT",EDGE,{"disambiguationData":[TD([[subQ2,-1.0]])],"derivedFrom":subQ1}),1.0]])]});}
            var Q62;
            {var subQ0=sQuery(id+"F0.wireOp",EDGE,"E18");var subQ1=sQuery(id+"F0.wireOp",EDGE,"E12");var subQ2=makeQuery(id+"F0.imprint","INTERSECT",VERTEX,{"derivedFrom":[subQ1,subQ0]});Q62=makeQuery(id+"F0.imprint","IMPRINT",FACE,{"disambiguationData":[TD([[makeQuery(id+"F0.imprint","IMPRINT",EDGE,{"disambiguationData":[TD([[subQ2,-1.0]])],"derivedFrom":subQ1}),1.0]])]});}
            var Q63;
            {var subQ0=sQuery(id+"F0.wireOp",EDGE,"E16");var subQ1=sQuery(id+"F0.wireOp",EDGE,"E10.left");var subQ2=makeQuery(id+"F0.imprint","INTERSECT",VERTEX,{"derivedFrom":[subQ1,subQ0]});Q63=makeQuery(id+"F0.imprint","IMPRINT",FACE,{"disambiguationData":[TD([[makeQuery(id+"F0.imprint","IMPRINT",EDGE,{"disambiguationData":[TD([[subQ2,1.0]])],"derivedFrom":subQ1}),-1.0]])]});}
            var Q64;
            {var subQ0=sQuery(id+"F0.wireOp",EDGE,"E18");var subQ1=sQuery(id+"F0.wireOp",EDGE,"E13");var subQ2=makeQuery(id+"F0.imprint","INTERSECT",VERTEX,{"derivedFrom":[subQ1,subQ0]});Q64=makeQuery(id+"F0.imprint","IMPRINT",FACE,{"disambiguationData":[TD([[makeQuery(id+"F0.imprint","IMPRINT",EDGE,{"disambiguationData":[TD([[subQ2,-1.0]])],"derivedFrom":subQ1}),1.0]])]});}
            var Q65;
            {var subQ0=sQuery(id+"F0.wireOp",EDGE,"E19");var subQ1=sQuery(id+"F0.wireOp",EDGE,"E12");var subQ2=makeQuery(id+"F0.imprint","INTERSECT",VERTEX,{"derivedFrom":[subQ1,subQ0]});Q65=makeQuery(id+"F0.imprint","IMPRINT",FACE,{"disambiguationData":[TD([[makeQuery(id+"F0.imprint","IMPRINT",EDGE,{"disambiguationData":[TD([[subQ2,-1.0]])],"derivedFrom":subQ1}),1.0]])]});}
            var Q66;
            {var subQ0=sQuery(id+"F0.wireOp",EDGE,"E18");var subQ1=sQuery(id+"F0.wireOp",EDGE,"E11");var subQ2=makeQuery(id+"F0.imprint","INTERSECT",VERTEX,{"derivedFrom":[subQ1,subQ0]});Q66=makeQuery(id+"F0.imprint","IMPRINT",FACE,{"disambiguationData":[TD([[makeQuery(id+"F0.imprint","IMPRINT",EDGE,{"disambiguationData":[TD([[subQ2,-1.0]])],"derivedFrom":subQ1}),1.0]])]});}
            var Q67;
            {var subQ0=sQuery(id+"F0.wireOp",EDGE,"E22");var subQ1=sQuery(id+"F0.wireOp",EDGE,"E14");var subQ2=makeQuery(id+"F0.imprint","INTERSECT",VERTEX,{"derivedFrom":[subQ1,subQ0]});Q67=makeQuery(id+"F0.imprint","IMPRINT",FACE,{"disambiguationData":[TD([[makeQuery(id+"F0.imprint","IMPRINT",EDGE,{"disambiguationData":[TD([[subQ2,-1.0]])],"derivedFrom":subQ1}),-1.0]])]});}
            var Q68;
            {var subQ0=sQuery(id+"F0.wireOp",EDGE,"E19");var subQ1=sQuery(id+"F0.wireOp",EDGE,"E13");var subQ2=makeQuery(id+"F0.imprint","INTERSECT",VERTEX,{"derivedFrom":[subQ1,subQ0]});Q68=makeQuery(id+"F0.imprint","IMPRINT",FACE,{"disambiguationData":[TD([[makeQuery(id+"F0.imprint","IMPRINT",EDGE,{"disambiguationData":[TD([[subQ2,-1.0]])],"derivedFrom":subQ1}),1.0]])]});}
            var Q69;
            {var subQ0=sQuery(id+"F0.wireOp",EDGE,"E17");var subQ1=sQuery(id+"F0.wireOp",EDGE,"E10.left");var subQ2=makeQuery(id+"F0.imprint","INTERSECT",VERTEX,{"derivedFrom":[subQ1,subQ0]});Q69=makeQuery(id+"F0.imprint","IMPRINT",FACE,{"disambiguationData":[TD([[makeQuery(id+"F0.imprint","IMPRINT",EDGE,{"disambiguationData":[TD([[subQ2,1.0]])],"derivedFrom":subQ1}),-1.0]])]});}
            extrude(context, id + "F1", {"entities" : qUnion([Q0, Q1, Q2, Q3, Q4, Q5, Q6, Q7, Q8, Q9, Q10, Q11, Q12, Q13, Q14, Q15, Q16, Q17, Q18, Q19, Q20, Q21, Q22, Q23, Q24, Q25, Q26, Q27, Q28, Q29, Q30, Q31, Q32, Q33, Q34, Q35, Q36, Q37, Q38, Q39, Q40, Q41, Q42, Q43, Q44, Q45, Q46, Q47, Q48, Q49, Q50, Q51, Q52, Q53, Q54, Q55, Q56, Q57, Q58, Q59, Q60, Q61, Q62, Q63, Q64, Q65, Q66, Q67, Q68, Q69]), "depth" : 50 * mm});
        }
    });
